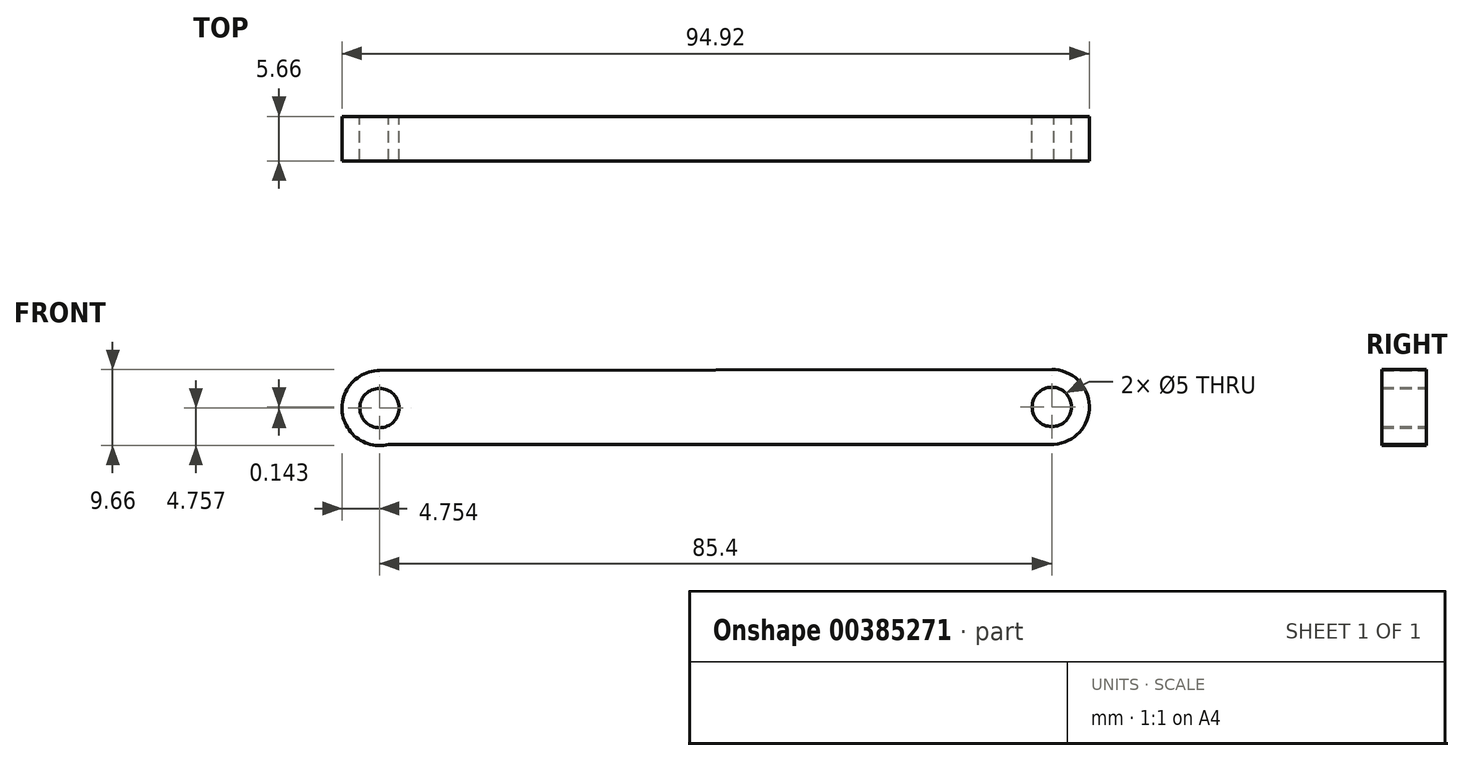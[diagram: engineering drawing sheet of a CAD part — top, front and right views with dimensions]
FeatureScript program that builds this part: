
annotation { "Feature Type Name" : "Feature", "Feature Type Description" : "" }
export const myFeature = defineFeature(function(context is Context, id is Id, definition is map)
    precondition{}
    {
        {
            var Q0;
            Q0=qCreatedBy(makeId("Front.planeOp"),FACE);
            var sketch = newSketch(context, id + "F0", { "sketchPlane" : qUnion([Q0])});
            skCircle(sketch, "E0", {"center": v(-43.12, -0.14) * mm, "radius": 2.5 * mm});
            skCircle(sketch, "E1", {"center": v(42.28, 0) * mm, "radius": 2.5 * mm});
            skArc(sketch, "E2", {"start": v(-43.1, 4.61) * mm, "mid": v(-47.84, -0.72) * mm, "end": v(-41.95, -4.75) * mm});
            skArc(sketch, "E3", {"start": v(42.56, -4.75) * mm, "mid": v(47.04, 0.14) * mm, "end": v(42.28, 4.76) * mm});
            skLineSegment(sketch, "E4", {"start": v(-43.1, 4.61) * mm, "end": v(42.28, 4.76) * mm});
            skLineSegment(sketch, "E5", {"start": v(-41.95, -4.75) * mm, "end": v(42.56, -4.75) * mm});
            skSolve(sketch);
        }
        {
            var Q0;
            Q0=makeQuery(id+"F0.imprint","IMPRINT",FACE,{"disambiguationData":[TD([[makeQuery(id+"F0.imprint","IMPRINT",EDGE,{"derivedFrom":sQuery(id+"F0.wireOp",EDGE,"E0")}),-1.0]])]});
            extrude(context, id + "F1", {"entities" : qUnion([Q0]), "depth" : 5.66 * mm});
        }
    });
